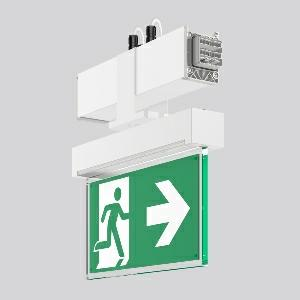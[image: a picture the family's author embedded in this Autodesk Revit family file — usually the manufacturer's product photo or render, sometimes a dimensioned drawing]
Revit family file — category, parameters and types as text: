
# Revit family: linedo_module_rz_9503rz_762_409_030_1df8
name_source: partatom
category: Lighting Fixtures
units: mm (PartAtom-declared; Revit-internal decimal feet)

## family parameters
Cut with Voids When Loaded = No
Host = Face
Light Source = No
Part Type = Normal
Room Calculation Point = No
Round Connector Dimension = Use Diameter
Shared = No

## types (1)
- LINEDO Module RZ
    Apparent Load = 0 VA
    Default Elevation = 1800 mm
    Description = LINEDO, white, on/off
Continuous line luminaire, L 336 B 62 H 343, CBS, AC-Control
    Height = 343 mm
    Lamp = 0 x
    Length = 336 mm
    Luminous efficacy = 0 lm/W
    Manufacturer = RZB
    ModVariant = No
    Model = 9503RZ.762.409.030
    Mounting Place = Ceiling
    Mounting Type = Surface mounted
    Number of Poles = 1
    OnlyDefault = Yes
    Power Factor = 1
    Product Name = LINEDO Module RZ
    Product group = Continuous line luminaire system Linedo IP 54
    ProductGroupID = 314
    Protection Class = Protection class I
    Protection Degree = IP 54
    RLX_Detail_Level = 1
    RLX_Emergency_Light_Flux = 0 lm
    RLX_Emergency_Type = 0
    RLX_Emergency_Type_DB = No
    RlxData = <blob elided: 35705 chars, md5=3f525c3b>
    Standby Power = 0 W
    System Light Flux = 0 lm
    System Power = 0 W
    Type Comments = Product without accessories
    Type Image = 9503rz.762.434.030.jpg
    URL = http://relux.com
    VarID = ---
    Voltage = 0 V
    Weight = 0.00 kg
    Width = 62 mm

## geometry (parser evidence)
native form markers: Blend x4, Sweep x12
no freeform markers — native parametric forms only
